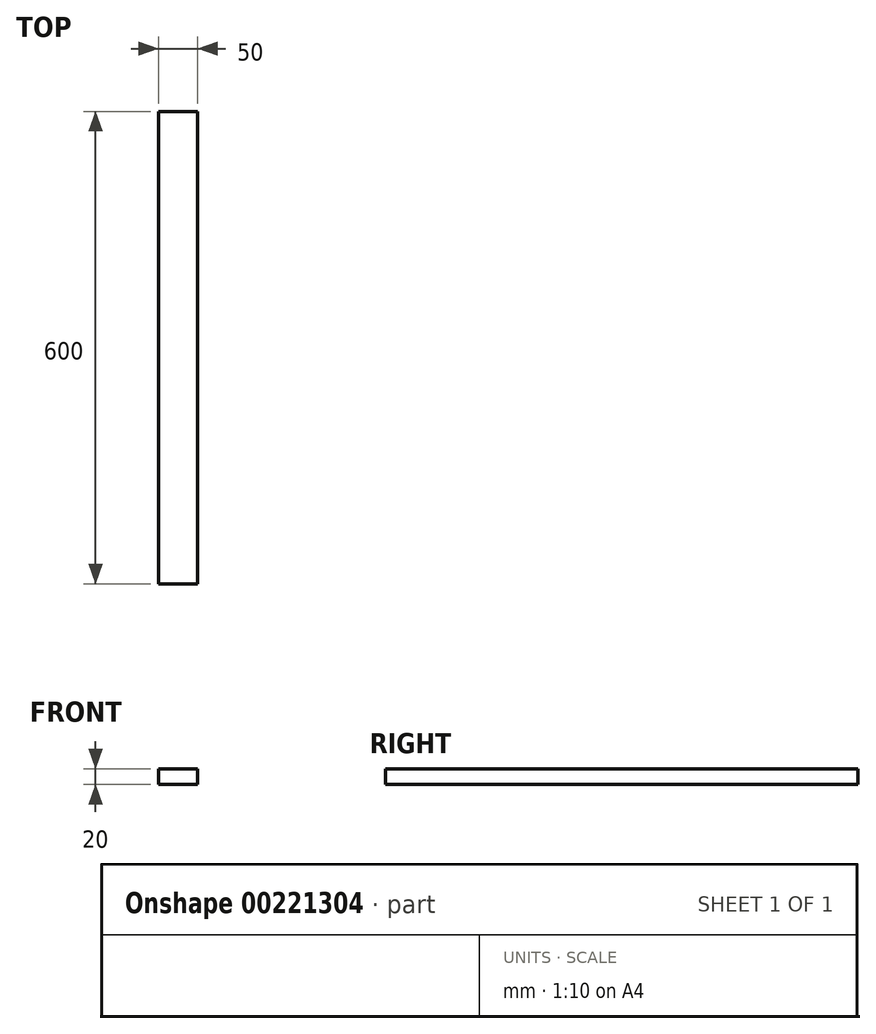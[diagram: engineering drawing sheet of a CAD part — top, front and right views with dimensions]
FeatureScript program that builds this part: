
annotation { "Feature Type Name" : "Feature", "Feature Type Description" : "" }
export const myFeature = defineFeature(function(context is Context, id is Id, definition is map)
    precondition{}
    {
        {
            var Q0;
            Q0=qCreatedBy(makeId("Front.planeOp"),FACE);
            var sketch = newSketch(context, id + "F0", { "sketchPlane" : qUnion([Q0])});
            skLineSegment(sketch, "E0.bottom", {"start": v(-21.52, 12.77) * mm, "end": v(28.48, 12.77) * mm});
            skLineSegment(sketch, "E0.top", {"start": v(-21.52, -7.23) * mm, "end": v(28.48, -7.23) * mm});
            skLineSegment(sketch, "E0.left", {"start": v(-21.52, 12.77) * mm, "end": v(-21.52, -7.23) * mm});
            skLineSegment(sketch, "E0.right", {"start": v(28.48, 12.77) * mm, "end": v(28.48, -7.23) * mm});
            skSolve(sketch);
        }
        {
            var Q0;
            Q0=makeQuery(id+"F0.imprint","IMPRINT",FACE,{"disambiguationData":[TD([[makeQuery(id+"F0.imprint","IMPRINT",EDGE,{"derivedFrom":sQuery(id+"F0.wireOp",EDGE,"E0.bottom")}),-1.0]])]});
            extrude(context, id + "F1", {"entities" : qUnion([Q0]), "oppositeDirection" : true, "depth" : 600 * mm});
        }
    });
